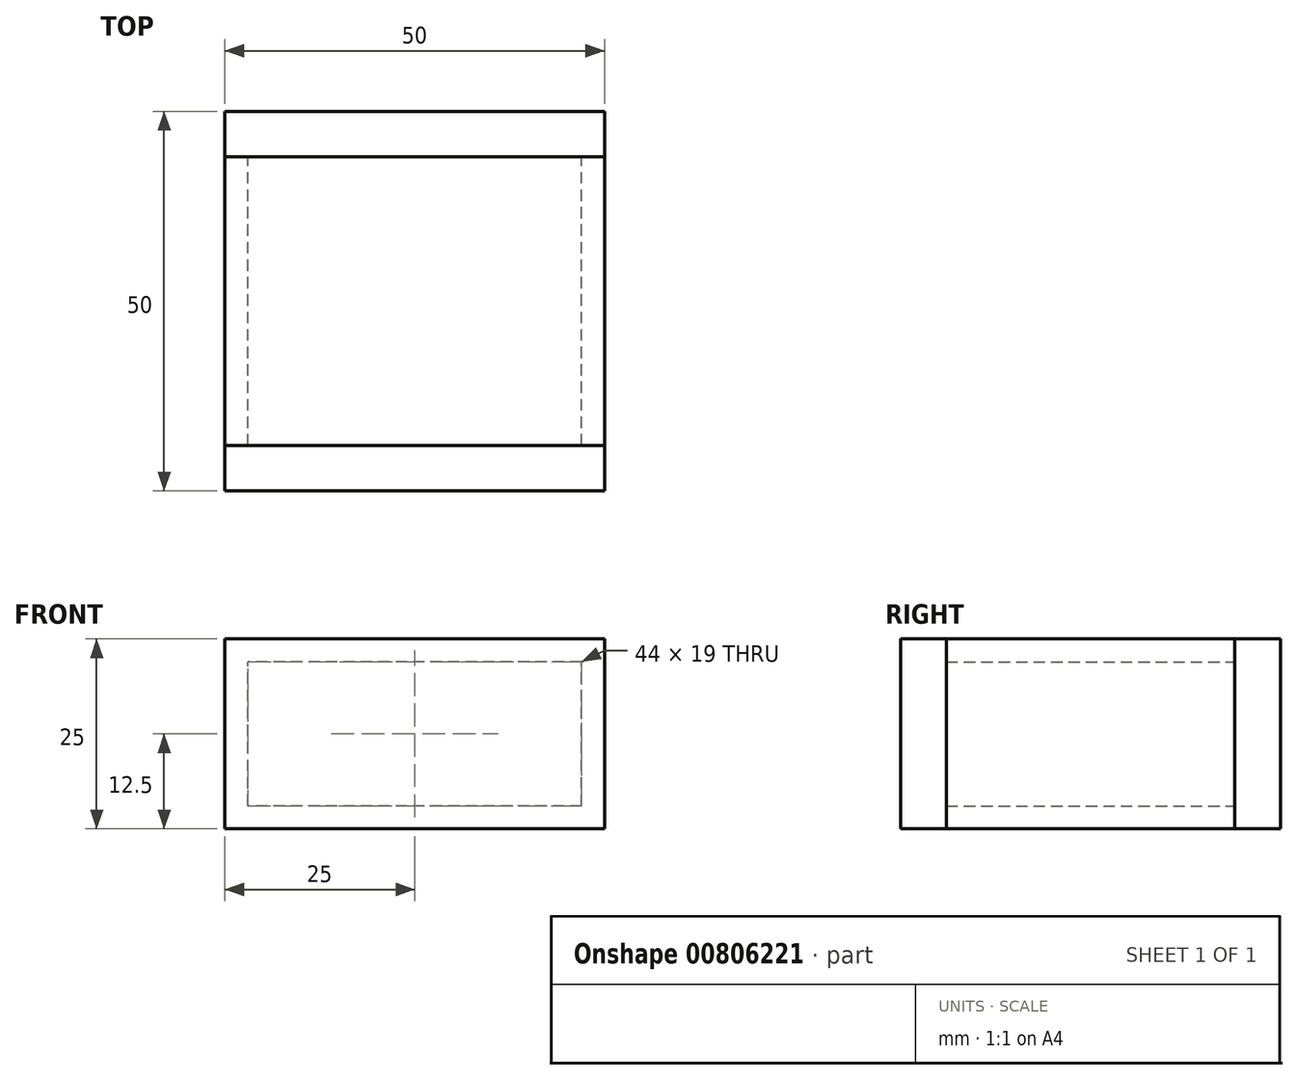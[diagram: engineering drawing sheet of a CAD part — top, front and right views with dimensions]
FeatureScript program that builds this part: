
annotation { "Feature Type Name" : "Feature", "Feature Type Description" : "" }
export const myFeature = defineFeature(function(context is Context, id is Id, definition is map)
    precondition{}
    {
        {
            var Q0;
            Q0=qCreatedBy(makeId("Front.planeOp"),FACE);
            var sketch = newSketch(context, id + "F0", { "sketchPlane" : qUnion([Q0])});
            skLineSegment(sketch, "E0.bottom", {"start": v(25, -12.5) * mm, "end": v(-25, -12.5) * mm});
            skLineSegment(sketch, "E0.top", {"start": v(25, 12.5) * mm, "end": v(-25, 12.5) * mm});
            skLineSegment(sketch, "E0.left", {"start": v(25, -12.5) * mm, "end": v(25, 12.5) * mm});
            skLineSegment(sketch, "E0.right", {"start": v(-25, -12.5) * mm, "end": v(-25, 12.5) * mm});
            skPoint(sketch, "E0.middle", {"position": v(0, 0) * mm});
            skLineSegment(sketch, "E1.0", {"start": v(22, 9.5) * mm, "end": v(-22, 9.5) * mm});
            skLineSegment(sketch, "E1.1", {"start": v(22, -9.5) * mm, "end": v(22, 9.5) * mm});
            skLineSegment(sketch, "E1.2", {"start": v(22, -9.5) * mm, "end": v(-22, -9.5) * mm});
            skLineSegment(sketch, "E1.3", {"start": v(-22, -9.5) * mm, "end": v(-22, 9.5) * mm});
            skSolve(sketch);
        }
        {
            var Q0;
            Q0=qSketchRegion(id+"F0",true);
            extrude(context, id + "F1", {"entities" : qUnion([Q0]), "depth" : 38 * mm, "offsetDistance" : 25 * mm});
        }
        {
            var Q0;
            Q0=makeQuery(id+"F1.opExtrude","CAP_FACE",FACE,{"disambiguationData":[OSD([sQuery(id+"F0.wireOp",EDGE,"E0.bottom"),sQuery(id+"F0.wireOp",EDGE,"E0.top"),sQuery(id+"F0.wireOp",EDGE,"E0.left"),sQuery(id+"F0.wireOp",EDGE,"E0.right"),sQuery(id+"F0.wireOp",EDGE,"E1.0"),sQuery(id+"F0.wireOp",EDGE,"E1.1"),sQuery(id+"F0.wireOp",EDGE,"E1.2"),sQuery(id+"F0.wireOp",EDGE,"E1.3")])],"isStart":false});
            var sketch = newSketch(context, id + "F2", { "sketchPlane" : qUnion([Q0])});
            skLineSegment(sketch, "E2.bottom", {"start": v(25, 12.5) * mm, "end": v(-25, 12.5) * mm});
            skLineSegment(sketch, "E2.top", {"start": v(25, -12.5) * mm, "end": v(-25, -12.5) * mm});
            skLineSegment(sketch, "E2.left", {"start": v(25, 12.5) * mm, "end": v(25, -12.5) * mm});
            skLineSegment(sketch, "E2.right", {"start": v(-25, 12.5) * mm, "end": v(-25, -12.5) * mm});
            skSolve(sketch);
        }
        {
            var Q0;
            Q0=qSketchRegion(id+"F2",true);
            extrude(context, id + "F3", {"entities" : qUnion([Q0]), "depth" : 6 * mm, "offsetDistance" : 25 * mm});
        }
        {
            var Q0;
            Q0=makeQuery(id+"F1.opExtrude","CAP_FACE",FACE,{"disambiguationData":[OSD([sQuery(id+"F0.wireOp",EDGE,"E0.bottom"),sQuery(id+"F0.wireOp",EDGE,"E0.top"),sQuery(id+"F0.wireOp",EDGE,"E0.left"),sQuery(id+"F0.wireOp",EDGE,"E0.right"),sQuery(id+"F0.wireOp",EDGE,"E1.0"),sQuery(id+"F0.wireOp",EDGE,"E1.1"),sQuery(id+"F0.wireOp",EDGE,"E1.2"),sQuery(id+"F0.wireOp",EDGE,"E1.3")])],"isStart":true});
            var sketch = newSketch(context, id + "F4", { "sketchPlane" : qUnion([Q0])});
            skLineSegment(sketch, "E3.bottom", {"start": v(-25, 12.5) * mm, "end": v(25, 12.5) * mm});
            skLineSegment(sketch, "E3.top", {"start": v(-25, -12.5) * mm, "end": v(25, -12.5) * mm});
            skLineSegment(sketch, "E3.left", {"start": v(-25, 12.5) * mm, "end": v(-25, -12.5) * mm});
            skLineSegment(sketch, "E3.right", {"start": v(25, 12.5) * mm, "end": v(25, -12.5) * mm});
            skSolve(sketch);
        }
        {
            var Q0;
            Q0=qSketchRegion(id+"F4",true);
            extrude(context, id + "F5", {"entities" : qUnion([Q0]), "depth" : 6 * mm, "offsetDistance" : 25 * mm});
        }
    });
